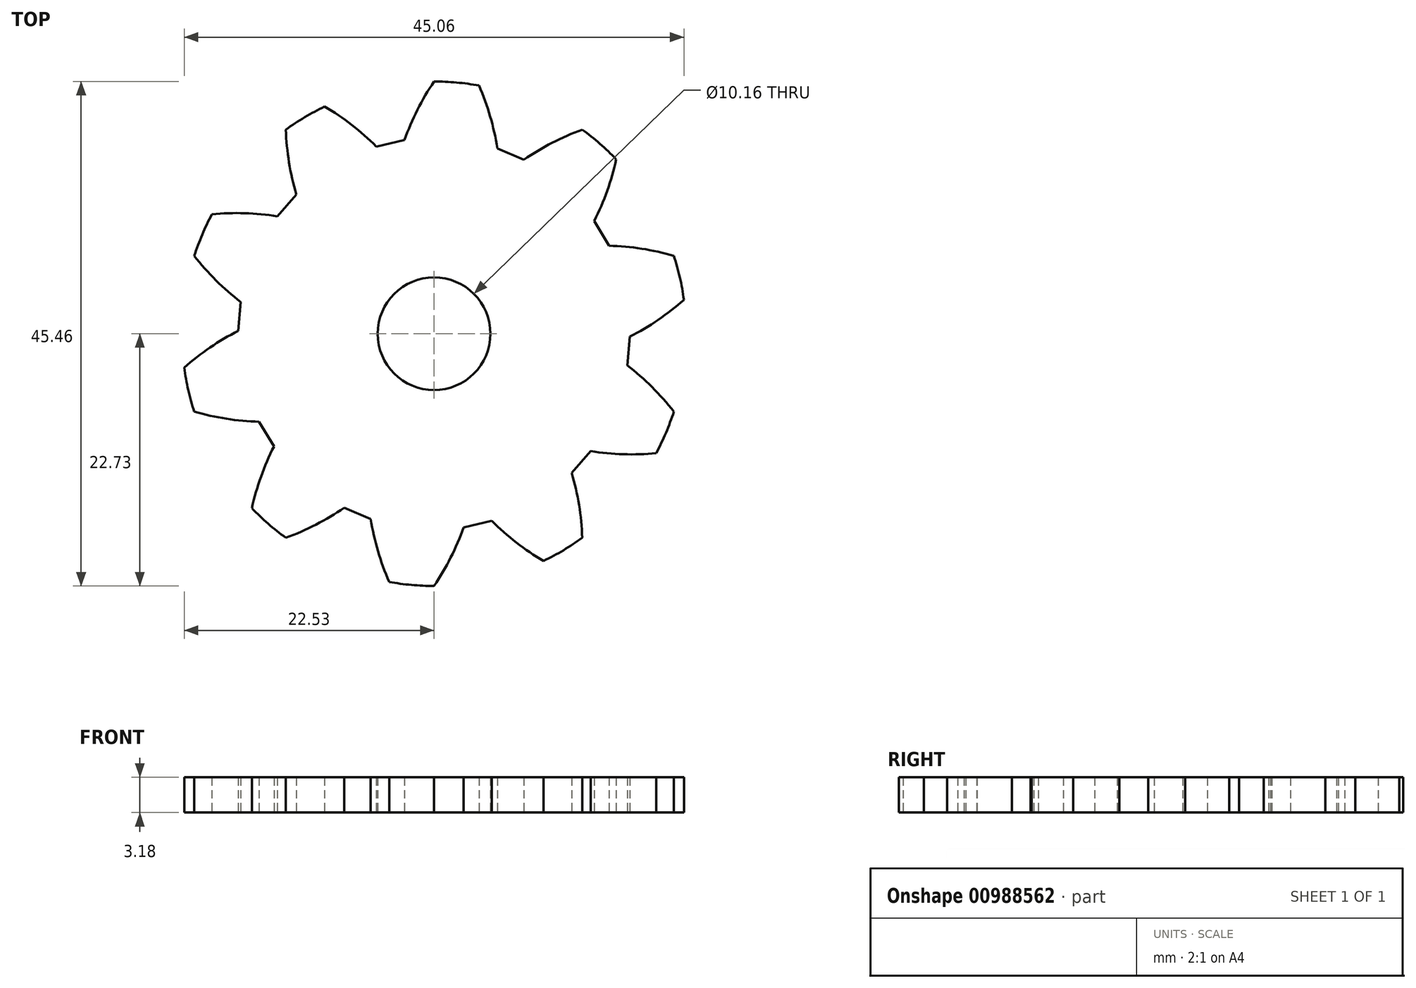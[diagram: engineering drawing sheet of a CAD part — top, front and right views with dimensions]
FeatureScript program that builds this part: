
annotation { "Feature Type Name" : "Feature", "Feature Type Description" : "" }
export const myFeature = defineFeature(function(context is Context, id is Id, definition is map)
    precondition{}
    {
        {
            var Q0;
            Q0=qCreatedBy(makeId("Right.planeOp"),FACE);
            var sketch = newSketch(context, id + "F0", { "sketchPlane" : qUnion([Q0])});
            skLineSegment(sketch, "E0", {"start": v(0, 0) * mm, "end": v(0, -73.7) * mm, "construction": true});
            skSolve(sketch);
        }
        {
            var Q0;
            Q0=qCreatedBy(makeId("Top.planeOp"),FACE);
            var sketch = newSketch(context, id + "F1", { "sketchPlane" : qUnion([Q0])});
            skCircle(sketch, "E1", {"center": v(0, 0) * mm, "radius": 20.2 * mm, "construction": true});
            skLineSegment(sketch, "E2", {"start": v(0, 0) * mm, "end": v(0, 20.2) * mm, "construction": true});
            skCircle(sketch, "E3", {"center": v(0, 0) * mm, "radius": 17.65 * mm});
            skCircle(sketch, "E4", {"center": v(0, 0) * mm, "radius": 22.73 * mm});
            skArc(sketch, "E5", {"start": v(-5.2, 16.87) * mm, "mid": v(-7.42, 18.82) * mm, "end": v(-9.87, 20.48) * mm});
            skLineSegment(sketch, "E6", {"start": v(-5.2, 16.87) * mm, "end": v(-2.66, 17.45) * mm});
            skLineSegment(sketch, "E7", {"start": v(0, 0) * mm, "end": v(-5.08, 22.16) * mm, "construction": true});
            skCircle(sketch, "E8", {"center": v(0, 0) * mm, "radius": 5.08 * mm});
            skArc(sketch, "E9", {"start": v(0, 22.73) * mm, "mid": v(-1.5, 20.18) * mm, "end": v(-2.66, 17.45) * mm});
            skSolve(sketch);
        }
        {
            var Q0;
            {var subQ1=sQuery(id+"F1.wireOp",EDGE,"E5");Q0=makeQuery(id+"F1.imprint","IMPRINT",FACE,{"disambiguationData":[TD([[makeQuery(id+"F1.imprint","IMPRINT",EDGE,{"derivedFrom":subQ1}),1.0]])]});}
            var Q1;
            {var subQ0=sQuery(id+"F1.wireOp",EDGE,"E6");Q1=makeQuery(id+"F1.imprint","IMPRINT",FACE,{"disambiguationData":[TD([[makeQuery(id+"F1.imprint","IMPRINT",EDGE,{"derivedFrom":subQ0}),-1.0]])]});}
            extrude(context, id + "F2", {"entities" : qUnion([Q0, Q1]), "depth" : 3.17 * mm, "offsetDistance" : 25.4 * mm});
        }
        {
            var Q0;
            Q0=makeQuery(id+"F2.opExtrude","SWEPT_FACE",FACE,{"disambiguationData":[OSD([sQuery(id+"F1.wireOp",EDGE,"E5")])]});
            var Q1;
            Q1=makeQuery(id+"F2.opExtrude","SWEPT_FACE",FACE,{"disambiguationData":[OSD([sQuery(id+"F1.wireOp",EDGE,"E6")])]});
            var Q2;
            Q2=makeQuery(id+"F2.opExtrude","SWEPT_FACE",FACE,{"disambiguationData":[OSD([sQuery(id+"F1.wireOp",EDGE,"E9")])]});
            var Q3;
            Q3=sQuery(id+"F0.wireOp",EDGE,"E0");
            circularPattern(context, id + "F3", {"patternType" : PatternType.FACE, "faces" : qUnion([Q0, Q1, Q2]), "axis" : qUnion([Q3]), "angle" : 360 * degree, "instanceCount" : 10, "equalSpace" : true});
        }
    });
